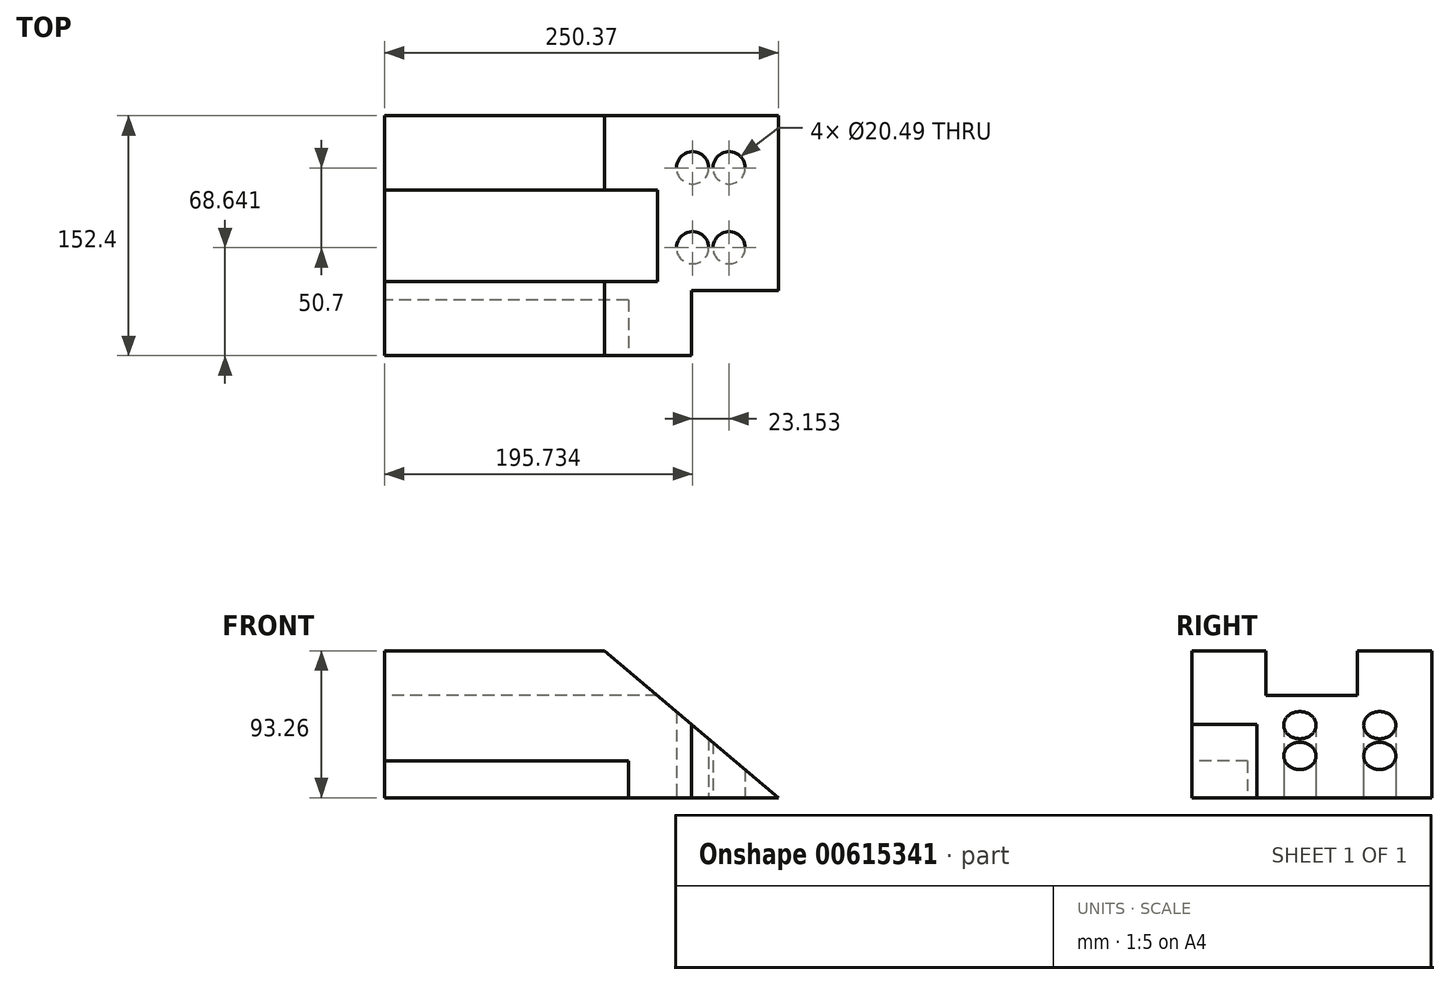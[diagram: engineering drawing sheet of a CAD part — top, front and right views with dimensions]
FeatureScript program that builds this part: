
annotation { "Feature Type Name" : "Feature", "Feature Type Description" : "" }
export const myFeature = defineFeature(function(context is Context, id is Id, definition is map)
    precondition{}
    {
        {
            var Q0;
            Q0=qCreatedBy(makeId("Front.planeOp"),FACE);
            var sketch = newSketch(context, id + "F0", { "sketchPlane" : qUnion([Q0])});
            skLineSegment(sketch, "E0.bottom", {"start": v(-69.9, 46.63) * mm, "end": v(69.9, 46.63) * mm});
            skLineSegment(sketch, "E0.top", {"start": v(-69.9, -46.63) * mm, "end": v(69.9, -46.63) * mm});
            skLineSegment(sketch, "E0.left", {"start": v(-69.9, 46.63) * mm, "end": v(-69.9, -46.63) * mm});
            skPoint(sketch, "E0.middle", {"position": v(0, 0) * mm});
            skPoint(sketch, "E1.end.orphan", {"position": v(69.9, -24.13) * mm});
            skLineSegment(sketch, "E2", {"start": v(69.9, 46.63) * mm, "end": v(180.46, -46.63) * mm});
            skLineSegment(sketch, "E3", {"start": v(180.46, -46.63) * mm, "end": v(69.9, -46.63) * mm});
            skSolve(sketch);
        }
        {
            var Q0;
            Q0=makeQuery(id+"F0.imprint","IMPRINT",FACE,{"disambiguationData":[TD([[makeQuery(id+"F0.imprint","IMPRINT",EDGE,{"derivedFrom":sQuery(id+"F0.wireOp",EDGE,"E0.bottom")}),-1.0]])]});
            extrude(context, id + "F1", {"entities" : qUnion([Q0]), "endBound" : BoundingType.SYMMETRIC, "depth" : 152.4 * mm, "offsetDistance" : 25.4 * mm});
        }
        {
            var Q0;
            Q0=makeQuery(id+"F1.opExtrude","SWEPT_FACE",FACE,{"disambiguationData":[OSD([sQuery(id+"F0.wireOp",EDGE,"E0.left")])]});
            var sketch = newSketch(context, id + "F2", { "sketchPlane" : qUnion([Q0])});
            skLineSegment(sketch, "E4.bottom", {"start": v(25.74, 22.86) * mm, "end": v(-25.74, 22.86) * mm});
            skPoint(sketch, "E4.middle", {"position": v(0, 46.63) * mm});
            skPoint(sketch, "E4.right.end.orphan", {"position": v(-25.74, 70.39) * mm});
            skPoint(sketch, "E4.left.end.orphan", {"position": v(25.74, 70.39) * mm});
            skSolve(sketch);
        }
        {
            var Q0;
            {var subQ0=sQuery(id+"F0.wireOp",EDGE,"E0.left");Q0=makeQuery(id+"F2.imprint","IMPRINT",FACE,{"disambiguationData":[TD([[makeQuery(id+"F2.imprint","IMPRINT",EDGE,{"derivedFrom":makeQuery(id+"F1.opExtrude","CAP_EDGE",EDGE,{"disambiguationData":[OSD([subQ0])],"isStart":true})}),1.0]])]});}
            var sketch = newSketch(context, id + "F3", { "sketchPlane" : qUnion([Q0])});
            skLineSegment(sketch, "E5.bottom", {"start": v(29.1, 18.26) * mm, "end": v(-29.1, 18.26) * mm});
            skLineSegment(sketch, "E5.top", {"start": v(29.1, 75.71) * mm, "end": v(-29.1, 75.71) * mm});
            skLineSegment(sketch, "E5.left", {"start": v(29.1, 18.26) * mm, "end": v(29.1, 75.71) * mm});
            skLineSegment(sketch, "E5.right", {"start": v(-29.1, 18.26) * mm, "end": v(-29.1, 75.71) * mm});
            skPoint(sketch, "E5.middle", {"position": v(0, 46.98) * mm});
            skSolve(sketch);
        }
        {
            var Q0;
            Q0 = qSketchRegion(id + "F3", true);
            extrude(context, id + "F4", {"entities" : qUnion([Q0]), "operationType" : NewBodyOperationType.REMOVE, "oppositeDirection" : true, "depth" : 215.14 * mm, "offsetDistance" : 25.4 * mm});
        }
        {
            var Q0;
            Q0=makeQuery(id+"F1.opExtrude","CAP_FACE",FACE,{"disambiguationData":[OSD([sQuery(id+"F0.wireOp",EDGE,"E0.bottom"),sQuery(id+"F0.wireOp",EDGE,"E0.top"),sQuery(id+"F0.wireOp",EDGE,"E0.left"),sQuery(id+"F0.wireOp",EDGE,"E2"),sQuery(id+"F0.wireOp",EDGE,"E3")])],"isStart":false});
            var sketch = newSketch(context, id + "F5", { "sketchPlane" : qUnion([Q0])});
            skLineSegment(sketch, "E6.bottom", {"start": v(115.37, 8.27) * mm, "end": v(185.94, 8.27) * mm});
            skLineSegment(sketch, "E6.top", {"start": v(115.37, -61.85) * mm, "end": v(185.94, -61.85) * mm});
            skLineSegment(sketch, "E6.left", {"start": v(115.37, 8.27) * mm, "end": v(115.37, -61.85) * mm});
            skLineSegment(sketch, "E6.right", {"start": v(185.94, 8.27) * mm, "end": v(185.94, -61.85) * mm});
            skSolve(sketch);
        }
        {
            var Q0;
            {var subQ4=sQuery(id+"F5.wireOp",EDGE,"E6.bottom");Q0=makeQuery(id+"F5.imprint","IMPRINT",FACE,{"disambiguationData":[TD([[makeQuery(id+"F5.imprint","IMPRINT",EDGE,{"derivedFrom":subQ4}),-1.0]])]});}
            extrude(context, id + "F6", {"entities" : qUnion([Q0]), "operationType" : NewBodyOperationType.REMOVE, "oppositeDirection" : true, "depth" : 154.7 * mm, "offsetDistance" : 25.4 * mm});
        }
        {
            var Q0;
            Q0=makeQuery(id+"F1.opExtrude","CAP_FACE",FACE,{"disambiguationData":[OSD([sQuery(id+"F0.wireOp",EDGE,"E0.bottom"),sQuery(id+"F0.wireOp",EDGE,"E0.top"),sQuery(id+"F0.wireOp",EDGE,"E0.left"),sQuery(id+"F0.wireOp",EDGE,"E2"),sQuery(id+"F0.wireOp",EDGE,"E3")])],"isStart":false});
            var sketch = newSketch(context, id + "F7", { "sketchPlane" : qUnion([Q0])});
            skLineSegment(sketch, "E7.bottom", {"start": v(125.18, 0) * mm, "end": v(182.06, 0) * mm});
            skLineSegment(sketch, "E7.top", {"start": v(125.18, -62.15) * mm, "end": v(182.06, -62.15) * mm});
            skLineSegment(sketch, "E7.left", {"start": v(125.18, 0) * mm, "end": v(125.18, -62.15) * mm});
            skLineSegment(sketch, "E7.right", {"start": v(182.06, 0) * mm, "end": v(182.06, -62.15) * mm});
            skSolve(sketch);
        }
        {
            var Q0;
            Q0 = qSketchRegion(id + "F7", true);
            extrude(context, id + "F8", {"entities" : qUnion([Q0]), "operationType" : NewBodyOperationType.REMOVE, "oppositeDirection" : true, "depth" : 41.4 * mm, "offsetDistance" : 25.4 * mm});
        }
        {
            var Q0;
            {var subQ0=sQuery(id+"F0.wireOp",EDGE,"E0.left");Q0=makeQuery(id+"F2.imprint","IMPRINT",FACE,{"disambiguationData":[TD([[makeQuery(id+"F2.imprint","IMPRINT",EDGE,{"derivedFrom":makeQuery(id+"F1.opExtrude","CAP_EDGE",EDGE,{"disambiguationData":[OSD([subQ0])],"isStart":true})}),1.0]])]});}
            var sketch = newSketch(context, id + "F9", { "sketchPlane" : qUnion([Q0])});
            skLineSegment(sketch, "E8.bottom", {"start": v(40.78, -23.36) * mm, "end": v(85.3, -23.36) * mm});
            skLineSegment(sketch, "E8.top", {"start": v(40.78, -58.77) * mm, "end": v(85.3, -58.77) * mm});
            skLineSegment(sketch, "E8.left", {"start": v(40.78, -23.36) * mm, "end": v(40.78, -58.77) * mm});
            skLineSegment(sketch, "E8.right", {"start": v(85.3, -23.36) * mm, "end": v(85.3, -58.77) * mm});
            skSolve(sketch);
        }
        {
            var Q0;
            Q0 = qSketchRegion(id + "F9", true);
            extrude(context, id + "F10", {"entities" : qUnion([Q0]), "operationType" : NewBodyOperationType.REMOVE, "oppositeDirection" : true, "depth" : 154.94 * mm, "offsetDistance" : 25.4 * mm});
        }
        {
            var Q0;
            Q0=makeQuery(id+"F1.opExtrude","SWEPT_FACE",FACE,{"disambiguationData":[OSD([sQuery(id+"F0.wireOp",EDGE,"E0.top"),sQuery(id+"F0.wireOp",EDGE,"E3")])]});
            var sketch = newSketch(context, id + "F11", { "sketchPlane" : qUnion([Q0])});
            skCircle(sketch, "E9", {"center": v(148.98, 7.56) * mm, "radius": 10.25 * mm});
            skCircle(sketch, "E10", {"center": v(148.98, -43.14) * mm, "radius": 10.25 * mm});
            skCircle(sketch, "E11", {"center": v(125.82, 7.56) * mm, "radius": 10.25 * mm});
            skCircle(sketch, "E12", {"center": v(125.82, -43.14) * mm, "radius": 10.25 * mm});
            skSolve(sketch);
        }
        {
            var Q0;
            Q0 = qSketchRegion(id + "F11", true);
            extrude(context, id + "F12", {"entities" : qUnion([Q0]), "operationType" : NewBodyOperationType.REMOVE, "endBound" : BoundingType.THROUGH_ALL, "oppositeDirection" : true, "depth" : 25.4 * mm, "offsetDistance" : 25.4 * mm});
        }
    });
